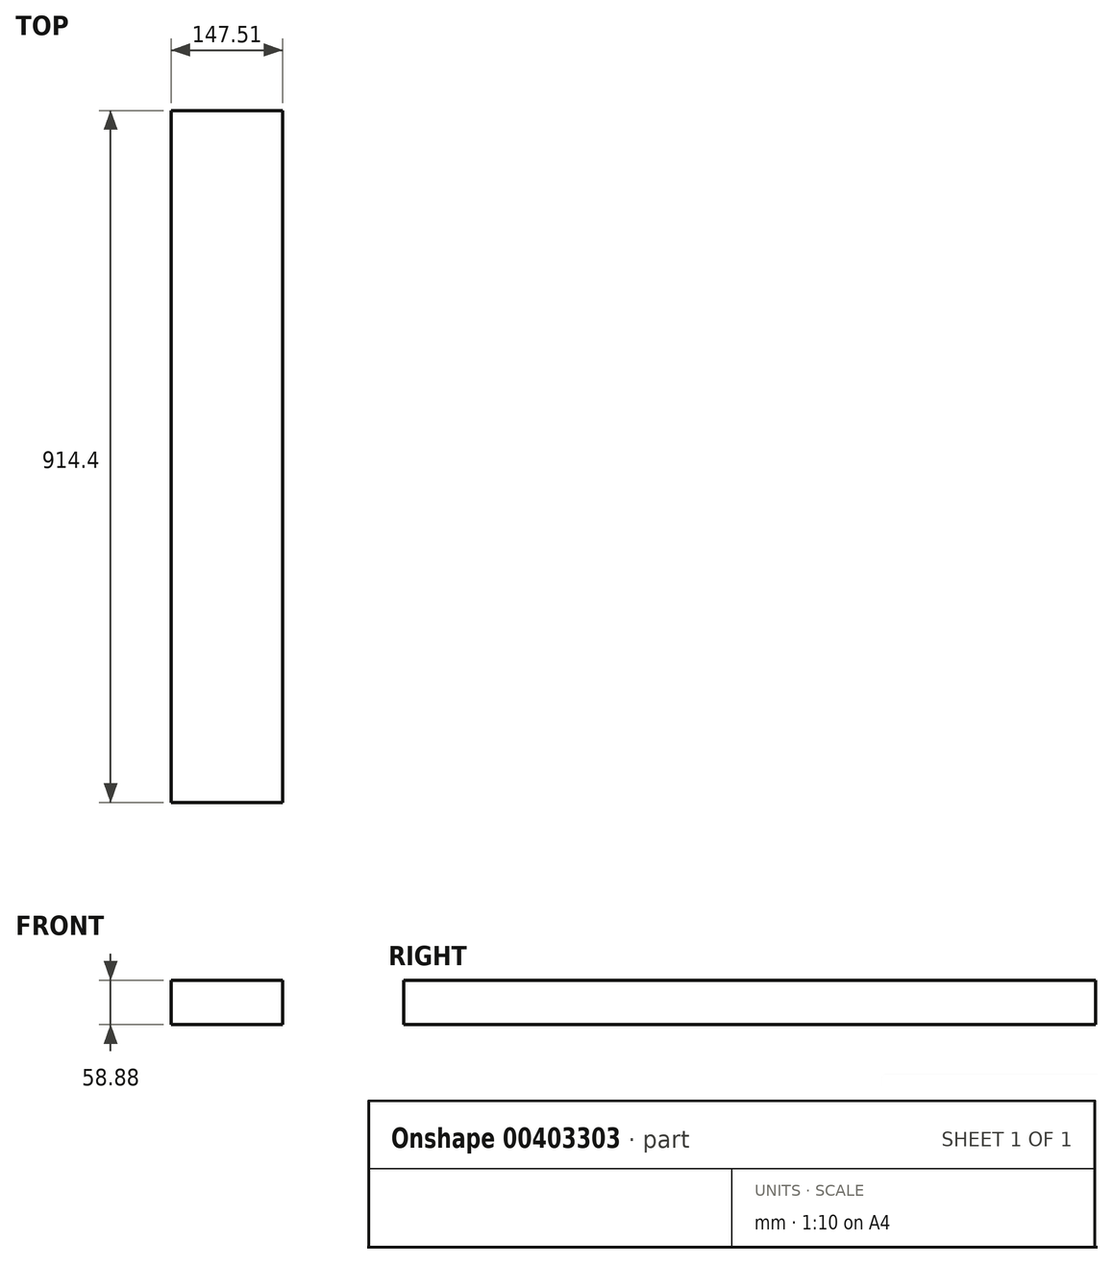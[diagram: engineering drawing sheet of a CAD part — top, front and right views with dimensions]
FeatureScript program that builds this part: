
annotation { "Feature Type Name" : "Feature", "Feature Type Description" : "" }
export const myFeature = defineFeature(function(context is Context, id is Id, definition is map)
    precondition{}
    {
        {
            var Q0;
            Q0=qCreatedBy(makeId("Front.planeOp"),FACE);
            var sketch = newSketch(context, id + "F0", { "sketchPlane" : qUnion([Q0])});
            skLineSegment(sketch, "E0.bottom", {"start": v(-73.97, 24.66) * mm, "end": v(73.54, 24.66) * mm});
            skLineSegment(sketch, "E0.top", {"start": v(-73.97, -34.22) * mm, "end": v(73.54, -34.22) * mm});
            skLineSegment(sketch, "E0.left", {"start": v(-73.97, 24.66) * mm, "end": v(-73.97, -34.22) * mm});
            skLineSegment(sketch, "E0.right", {"start": v(73.54, 24.66) * mm, "end": v(73.54, -34.22) * mm});
            skSolve(sketch);
        }
        {
            var Q0;
            Q0=makeQuery(id+"F0.imprint","IMPRINT",FACE,{"disambiguationData":[TD([[makeQuery(id+"F0.imprint","IMPRINT",EDGE,{"derivedFrom":sQuery(id+"F0.wireOp",EDGE,"E0.bottom")}),-1.0]])]});
            extrude(context, id + "F1", {"entities" : qUnion([Q0]), "depth" : 914.4 * mm});
        }
    });
